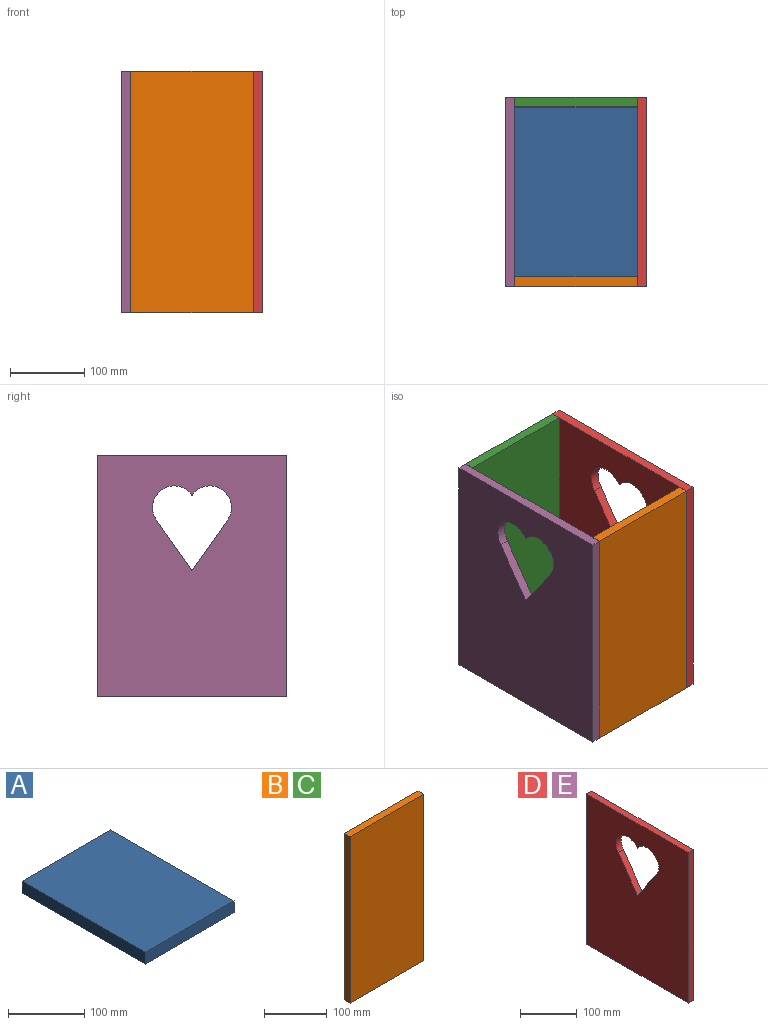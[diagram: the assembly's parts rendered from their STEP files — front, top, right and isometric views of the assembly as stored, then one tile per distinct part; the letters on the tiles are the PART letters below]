
ASSEMBLY  parts=5 mates=8
PART A: 6 faces, bbox 165.1x228.6x19.1 mm
  f0: plane 228.6x19.05mm, normal (-1,0,0), area 4354.8mm2, adj f1,f3,f4,f5
  f1: plane 165.1x19.05mm, normal (0,-1,0), area 3145.2mm2, adj f0,f2,f4,f5
  f2: plane 228.6x19.05mm, normal (1,0,0), area 4354.8mm2, adj f1,f3,f4,f5
  f3: plane 165.1x19.05mm, normal (0,1,0), area 3145.2mm2, adj f0,f2,f4,f5
  f4: plane 228.6x165.1mm, normal (0,0,1), area 37741.9mm2, adj f0,f1,f2,f3
  f5: plane 228.6x165.1mm, normal (0,0,-1), area 37741.9mm2, adj f0,f1,f2,f3
PART B: 6 faces, bbox 165.1x12.7x323.9 mm
  f0: plane 323.85x12.7mm, normal (-1,0,0), area 4112.9mm2, adj f1,f3,f4,f5
  f1: plane 165.1x12.7mm, normal (0,0,-1), area 2096.8mm2, adj f0,f2,f4,f5
  f2: plane 323.85x12.7mm, normal (1,0,0), area 4112.9mm2, adj f1,f3,f4,f5
  f3: plane 165.1x12.7mm, normal (0,0,1), area 2096.8mm2, adj f0,f2,f4,f5
  f4: plane 323.85x165.1mm, normal (0,-1,0), area 53467.6mm2, adj f0,f1,f2,f3
  f5: plane 323.85x165.1mm, normal (0,1,0), area 53467.6mm2, adj f0,f1,f2,f3
PART C: same geometry as B
PART D: 10 faces, bbox 12.7x254x323.9 mm
  f0: plane 323.85x12.7mm, normal (0,-1,0), area 4112.9mm2, adj f1,f3,f4,f5
  f1: plane 254x12.7mm, normal (0,0,-1), area 3225.8mm2, adj f0,f2,f4,f5
  f2: plane 323.85x12.7mm, normal (0,1,0), area 4112.9mm2, adj f1,f3,f4,f5
  f3: plane 254x12.7mm, normal (0,0,1), area 3225.8mm2, adj f0,f2,f4,f5
  f4: plane 323.85x254mm, normal (1,0,0), area 74740.7mm2, adj f0,f1,f2,f3,f6,f7,f8,f9
  f5: plane 323.85x254mm, normal (-1,0,0), area 74740.7mm2, adj f0,f1,f2,f3,f6,f7,f8,f9
  f6: plane 68.17x47.74mm, normal (0,0.82,0.57), area 1057mm2, adj f4,f5,f7,f9
  f7: plane 68.17x47.74mm, normal (0,-0.82,0.57), area 1057mm2, adj f4,f5,f6,f8
  f8: cylinder r=29.14mm len=53.01mm, axis (1,0,0), area 1162.5mm2, adj f4,f5,f7,f9
  f9: cylinder r=29.14mm len=53.01mm, axis (1,0,0), area 1162.5mm2, adj f4,f5,f6,f8
PART E: same geometry as D
PLACE A at identity fixed
PLACE B t=(0,-120.65,161.92)mm
PLACE C t=(0,120.65,161.92)mm
PLACE D t=(88.9,0,161.92)mm
PLACE E t=(-88.9,0,161.92)mm
MATE planar A.f0 <-> E.f4  axis (-1,0,0) through (-82.55,0,9.53)mm
MATE planar A.f5 <-> E.f1  axis (0,0,-1) through (0,0,0)mm
MATE planar A.f5 <-> B.f1  axis (0,0,-1) through (0,0,0)mm
MATE planar A.f2 <-> D.f5  axis (1,0,0) through (82.55,0,9.53)mm
MATE planar A.f1 <-> B.f5  axis (0,-1,0) through (0,-114.3,9.52)mm
MATE planar D.f1 <-> A.f5  axis (0,0,-1) through (88.9,0,0)mm
MATE planar A.f5 <-> C.f1  axis (0,0,-1) through (0,0,0)mm
MATE planar A.f3 <-> C.f4  axis (0,1,0) through (0,114.3,9.52)mm
